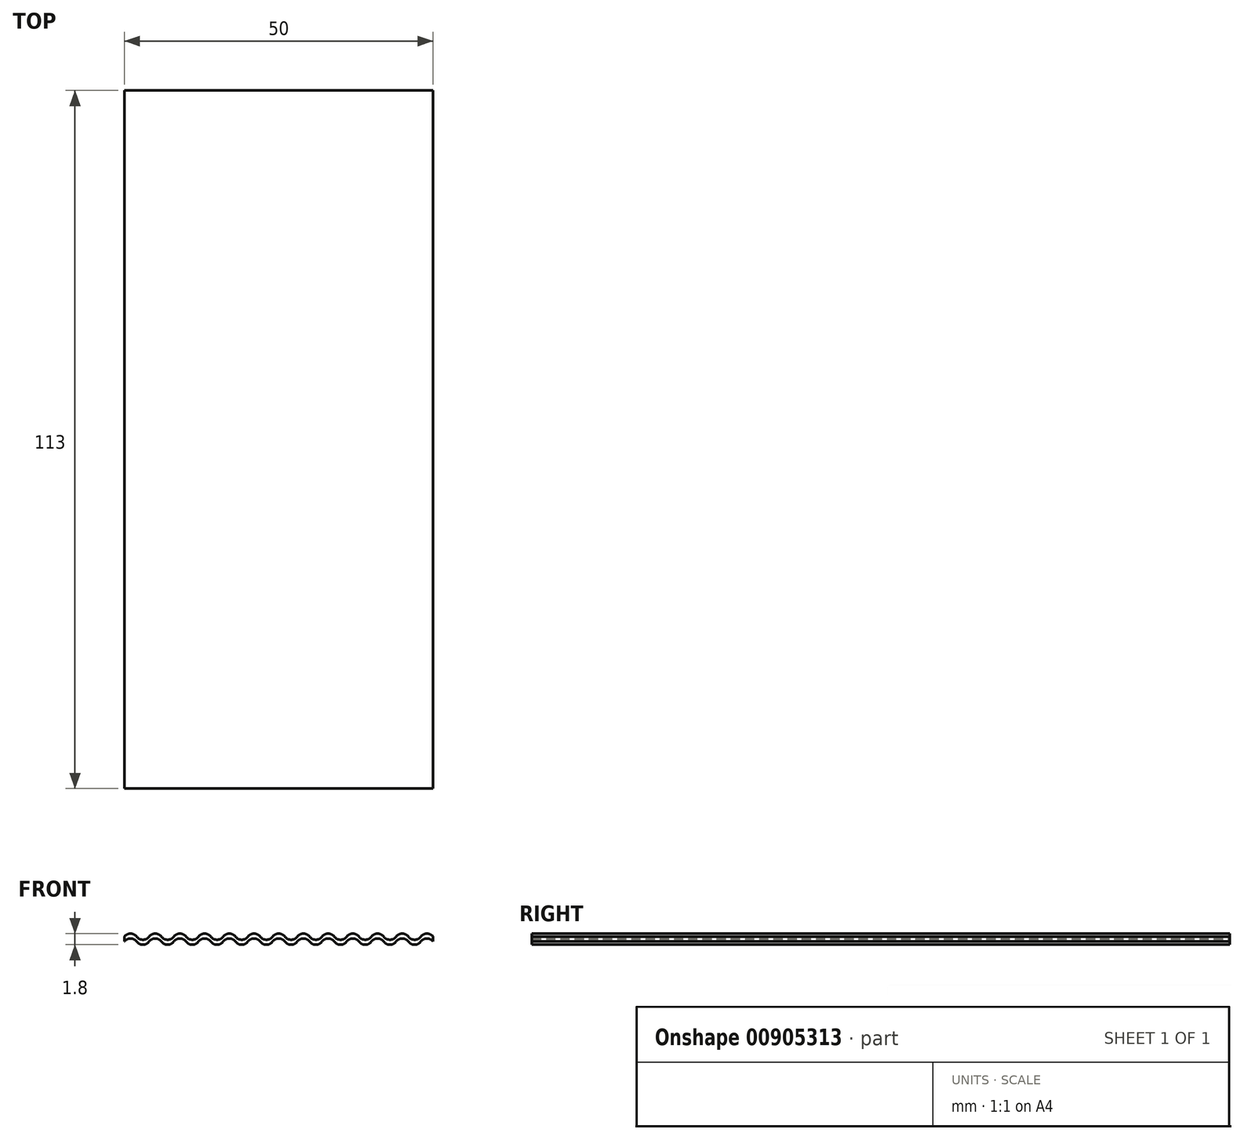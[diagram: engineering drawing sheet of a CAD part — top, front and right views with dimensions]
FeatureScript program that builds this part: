
annotation { "Feature Type Name" : "Feature", "Feature Type Description" : "" }
export const myFeature = defineFeature(function(context is Context, id is Id, definition is map)
    precondition{}
    {
        {
            var Q0;
            Q0=qCreatedBy(makeId("Front.planeOp"),FACE);
            var sketch = newSketch(context, id + "F0", { "sketchPlane" : qUnion([Q0])});
            skArc(sketch, "E0", {"start": v(-19, -0.4) * mm, "mid": v(-20, 0.1) * mm, "end": v(-21, -0.4) * mm});
            skArc(sketch, "E1", {"start": v(-23, -0.4) * mm, "mid": v(-22, -0.9) * mm, "end": v(-21, -0.4) * mm});
            skArc(sketch, "E2", {"start": v(-23, -0.4) * mm, "mid": v(-24, 0.1) * mm, "end": v(-25, -0.4) * mm});
            skArc(sketch, "E3", {"start": v(5, -0.4) * mm, "mid": v(6, -0.9) * mm, "end": v(7, -0.4) * mm});
            skArc(sketch, "E4", {"start": v(9, -0.4) * mm, "mid": v(8, 0.1) * mm, "end": v(7, -0.4) * mm});
            skArc(sketch, "E5", {"start": v(9, -0.4) * mm, "mid": v(10, -0.9) * mm, "end": v(11, -0.4) * mm});
            skArc(sketch, "E6", {"start": v(13, -0.4) * mm, "mid": v(12, 0.1) * mm, "end": v(11, -0.4) * mm});
            skArc(sketch, "E7", {"start": v(13, -0.4) * mm, "mid": v(14, -0.9) * mm, "end": v(15, -0.4) * mm});
            skArc(sketch, "E8", {"start": v(17, -0.4) * mm, "mid": v(16, 0.1) * mm, "end": v(15, -0.4) * mm});
            skArc(sketch, "E9", {"start": v(25, -0.4) * mm, "mid": v(24, 0.1) * mm, "end": v(23, -0.4) * mm});
            skArc(sketch, "E10", {"start": v(21, -0.4) * mm, "mid": v(22, -0.9) * mm, "end": v(23, -0.4) * mm});
            skArc(sketch, "E11", {"start": v(21, -0.4) * mm, "mid": v(20, 0.1) * mm, "end": v(19, -0.4) * mm});
            skArc(sketch, "E12", {"start": v(17, -0.4) * mm, "mid": v(18, -0.9) * mm, "end": v(19, -0.4) * mm});
            skArc(sketch, "E13", {"start": v(5, -0.4) * mm, "mid": v(4, 0.1) * mm, "end": v(3, -0.4) * mm});
            skArc(sketch, "E14", {"start": v(1, -0.4) * mm, "mid": v(2, -0.9) * mm, "end": v(3, -0.4) * mm});
            skArc(sketch, "E15", {"start": v(1, -0.4) * mm, "mid": v(0, 0.1) * mm, "end": v(-1, -0.4) * mm});
            skArc(sketch, "E16", {"start": v(-3, -0.4) * mm, "mid": v(-2, -0.9) * mm, "end": v(-1, -0.4) * mm});
            skArc(sketch, "E17", {"start": v(-3, -0.4) * mm, "mid": v(-4, 0.1) * mm, "end": v(-5, -0.4) * mm});
            skArc(sketch, "E18", {"start": v(-7, -0.4) * mm, "mid": v(-6, -0.9) * mm, "end": v(-5, -0.4) * mm});
            skArc(sketch, "E19", {"start": v(-7, -0.4) * mm, "mid": v(-8, 0.1) * mm, "end": v(-9, -0.4) * mm});
            skArc(sketch, "E20", {"start": v(-11, -0.4) * mm, "mid": v(-10, -0.9) * mm, "end": v(-9, -0.4) * mm});
            skArc(sketch, "E21", {"start": v(-11, -0.4) * mm, "mid": v(-12, 0.1) * mm, "end": v(-13, -0.4) * mm});
            skArc(sketch, "E22", {"start": v(-15, -0.4) * mm, "mid": v(-14, -0.9) * mm, "end": v(-13, -0.4) * mm});
            skArc(sketch, "E23", {"start": v(-15, -0.4) * mm, "mid": v(-16, 0.1) * mm, "end": v(-17, -0.4) * mm});
            skArc(sketch, "E24", {"start": v(-19, -0.4) * mm, "mid": v(-18, -0.9) * mm, "end": v(-17, -0.4) * mm});
            skArc(sketch, "E25", {"start": v(-19, 0.4) * mm, "mid": v(-20, 0.9) * mm, "end": v(-21, 0.4) * mm});
            skArc(sketch, "E26", {"start": v(-23, 0.4) * mm, "mid": v(-22, -0.1) * mm, "end": v(-21, 0.4) * mm});
            skArc(sketch, "E27", {"start": v(-23, 0.4) * mm, "mid": v(-24, 0.9) * mm, "end": v(-25, 0.4) * mm});
            skArc(sketch, "E28", {"start": v(5, 0.4) * mm, "mid": v(6, -0.1) * mm, "end": v(7, 0.4) * mm});
            skArc(sketch, "E29", {"start": v(9, 0.4) * mm, "mid": v(8, 0.9) * mm, "end": v(7, 0.4) * mm});
            skArc(sketch, "E30", {"start": v(9, 0.4) * mm, "mid": v(10, -0.1) * mm, "end": v(11, 0.4) * mm});
            skArc(sketch, "E31", {"start": v(13, 0.4) * mm, "mid": v(12, 0.9) * mm, "end": v(11, 0.4) * mm});
            skArc(sketch, "E32", {"start": v(13, 0.4) * mm, "mid": v(14, -0.1) * mm, "end": v(15, 0.4) * mm});
            skArc(sketch, "E33", {"start": v(17, 0.4) * mm, "mid": v(16, 0.9) * mm, "end": v(15, 0.4) * mm});
            skArc(sketch, "E34", {"start": v(25, 0.4) * mm, "mid": v(24, 0.9) * mm, "end": v(23, 0.4) * mm});
            skArc(sketch, "E35", {"start": v(21, 0.4) * mm, "mid": v(22, -0.1) * mm, "end": v(23, 0.4) * mm});
            skArc(sketch, "E36", {"start": v(21, 0.4) * mm, "mid": v(20, 0.9) * mm, "end": v(19, 0.4) * mm});
            skArc(sketch, "E37", {"start": v(17, 0.4) * mm, "mid": v(18, -0.1) * mm, "end": v(19, 0.4) * mm});
            skArc(sketch, "E38", {"start": v(5, 0.4) * mm, "mid": v(4, 0.9) * mm, "end": v(3, 0.4) * mm});
            skArc(sketch, "E39", {"start": v(1, 0.4) * mm, "mid": v(2, -0.1) * mm, "end": v(3, 0.4) * mm});
            skArc(sketch, "E40", {"start": v(1, 0.4) * mm, "mid": v(0, 0.9) * mm, "end": v(-1, 0.4) * mm});
            skArc(sketch, "E41", {"start": v(-3, 0.4) * mm, "mid": v(-2, -0.1) * mm, "end": v(-1, 0.4) * mm});
            skArc(sketch, "E42", {"start": v(-3, 0.4) * mm, "mid": v(-4, 0.9) * mm, "end": v(-5, 0.4) * mm});
            skArc(sketch, "E43", {"start": v(-7, 0.4) * mm, "mid": v(-6, -0.1) * mm, "end": v(-5, 0.4) * mm});
            skArc(sketch, "E44", {"start": v(-7, 0.4) * mm, "mid": v(-8, 0.9) * mm, "end": v(-9, 0.4) * mm});
            skArc(sketch, "E45", {"start": v(-11, 0.4) * mm, "mid": v(-10, -0.1) * mm, "end": v(-9, 0.4) * mm});
            skArc(sketch, "E46", {"start": v(-11, 0.4) * mm, "mid": v(-12, 0.9) * mm, "end": v(-13, 0.4) * mm});
            skArc(sketch, "E47", {"start": v(-15, 0.4) * mm, "mid": v(-14, -0.1) * mm, "end": v(-13, 0.4) * mm});
            skArc(sketch, "E48", {"start": v(-15, 0.4) * mm, "mid": v(-16, 0.9) * mm, "end": v(-17, 0.4) * mm});
            skArc(sketch, "E49", {"start": v(-19, 0.4) * mm, "mid": v(-18, -0.1) * mm, "end": v(-17, 0.4) * mm});
            skLineSegment(sketch, "E50", {"start": v(-25, 0.4) * mm, "end": v(-25, -0.4) * mm});
            skLineSegment(sketch, "E51", {"start": v(25, 0.4) * mm, "end": v(25, -0.4) * mm});
            skSolve(sketch);
        }
        {
            var Q0;
            Q0=qSketchRegion(id+"F0",true);
            extrude(context, id + "F1", {"entities" : qUnion([Q0]), "depth" : 113 * mm, "offsetDistance" : 25 * mm});
        }
    });
